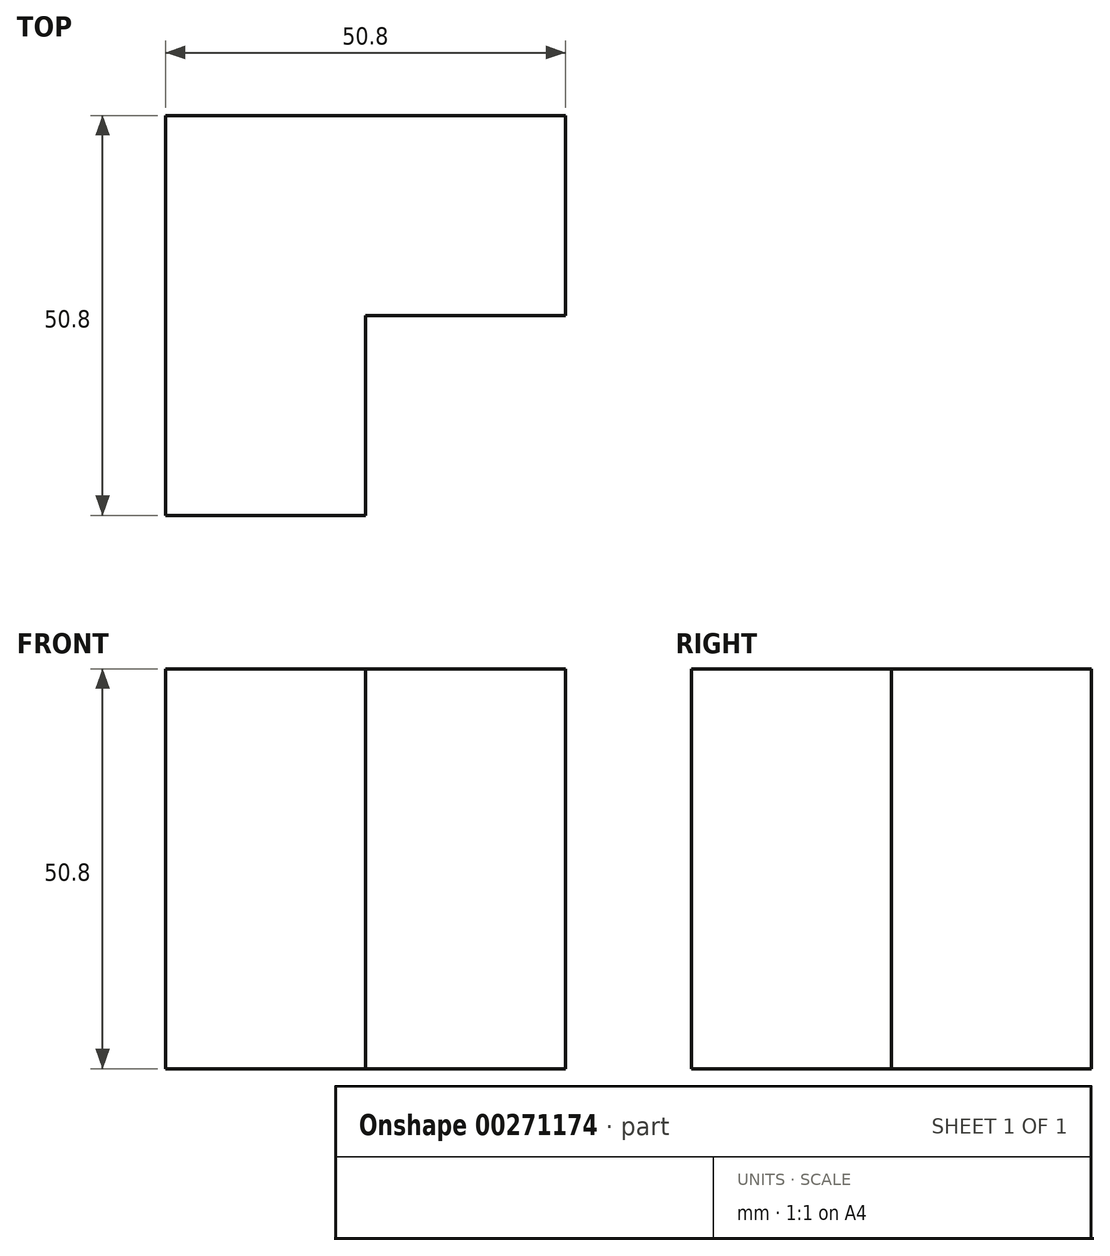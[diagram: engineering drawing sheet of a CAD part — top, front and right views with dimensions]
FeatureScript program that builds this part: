
annotation { "Feature Type Name" : "Feature", "Feature Type Description" : "" }
export const myFeature = defineFeature(function(context is Context, id is Id, definition is map)
    precondition{}
    {
        {
            var Q0;
            Q0=qCreatedBy(makeId("Front.planeOp"),FACE);
            var sketch = newSketch(context, id + "F0", { "sketchPlane" : qUnion([Q0])});
            skLineSegment(sketch, "E0.bottom", {"start": v(0, 0) * mm, "end": v(-50.8, 0) * mm});
            skLineSegment(sketch, "E0.top", {"start": v(0, 50.8) * mm, "end": v(-50.8, 50.8) * mm});
            skLineSegment(sketch, "E0.left", {"start": v(0, 0) * mm, "end": v(0, 50.8) * mm});
            skLineSegment(sketch, "E0.right", {"start": v(-50.8, 0) * mm, "end": v(-50.8, 50.8) * mm});
            skSolve(sketch);
        }
        {
            var Q0;
            Q0=makeQuery(id+"F0.imprint","IMPRINT",FACE,{"disambiguationData":[TD([[makeQuery(id+"F0.imprint","IMPRINT",EDGE,{"derivedFrom":sQuery(id+"F0.wireOp",EDGE,"E0.bottom")}),-1.0]])]});
            extrude(context, id + "F1", {"entities" : qUnion([Q0]), "depth" : 50.8 * mm});
        }
        {
            var Q0;
            Q0=makeQuery(id+"F1.opExtrude","SWEPT_FACE",FACE,{"disambiguationData":[OSD([sQuery(id+"F0.wireOp",EDGE,"E0.top")])]});
            var sketch = newSketch(context, id + "F2", { "sketchPlane" : qUnion([Q0])});
            skLineSegment(sketch, "E1", {"start": v(0, -50.8) * mm, "end": v(-25.4, -50.8) * mm});
            skLineSegment(sketch, "E2", {"start": v(-25.4, -50.8) * mm, "end": v(-25.4, -25.4) * mm});
            skLineSegment(sketch, "E3", {"start": v(-25.4, -25.4) * mm, "end": v(0, -25.4) * mm});
            skLineSegment(sketch, "E4", {"start": v(0, -25.4) * mm, "end": v(0, -50.8) * mm});
            skSolve(sketch);
        }
        {
            var Q0;
            Q0 = qSketchRegion(id + "F2", true);
            extrude(context, id + "F3", {"entities" : qUnion([Q0]), "operationType" : NewBodyOperationType.REMOVE, "oppositeDirection" : true, "depth" : 50.8 * mm});
        }
    });
